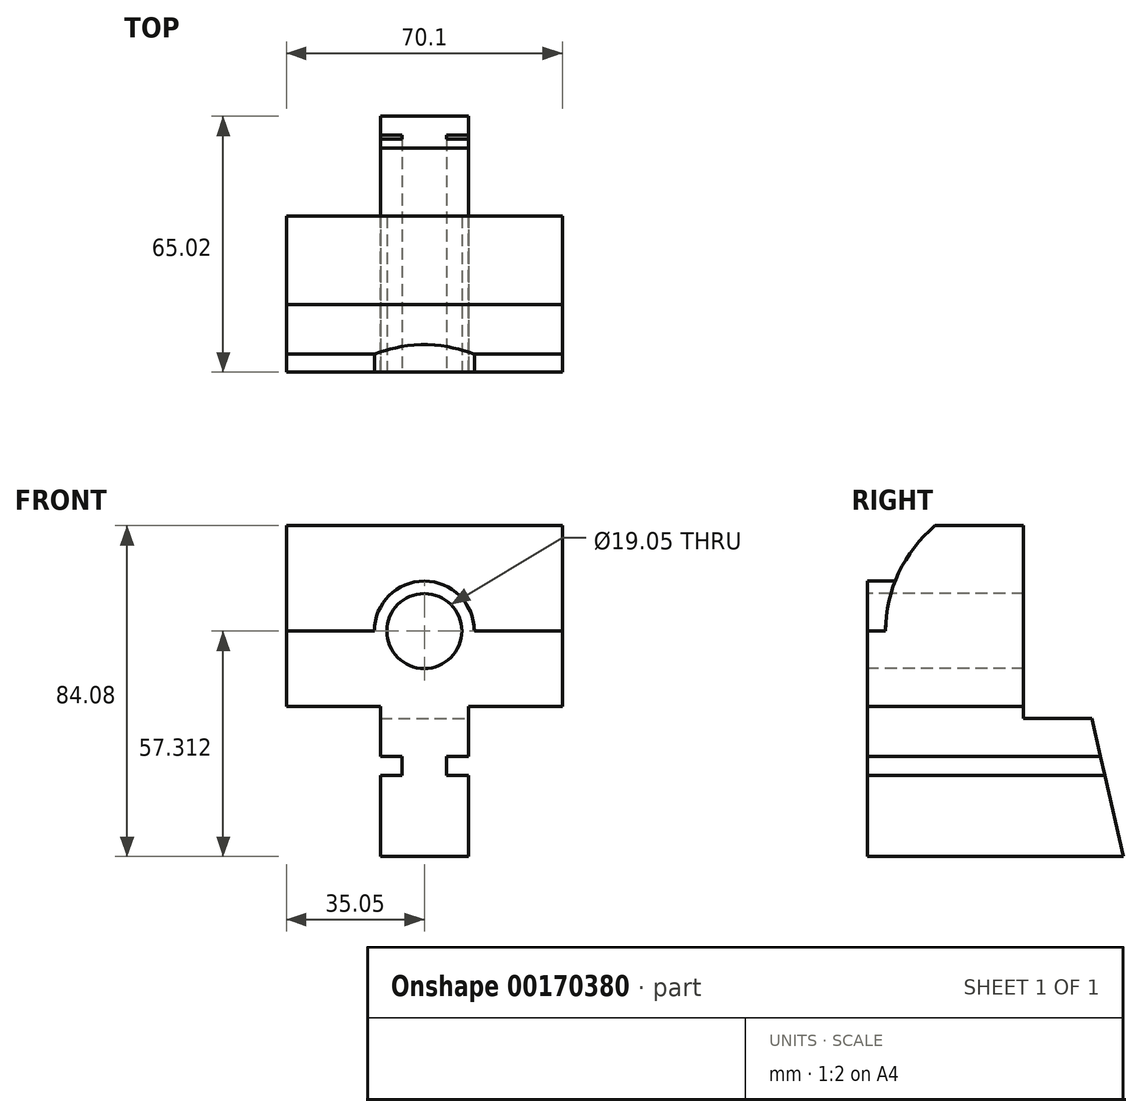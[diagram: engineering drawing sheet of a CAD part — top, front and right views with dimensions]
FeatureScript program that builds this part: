
annotation { "Feature Type Name" : "Feature", "Feature Type Description" : "" }
export const myFeature = defineFeature(function(context is Context, id is Id, definition is map)
    precondition{}
    {
        {
            var Q0;
            Q0=qCreatedBy(makeId("Right.planeOp"),FACE);
            var sketch = newSketch(context, id + "F0", { "sketchPlane" : qUnion([Q0])});
            skLineSegment(sketch, "E0.bottom", {"start": v(32.51, 42.04) * mm, "end": v(-32.51, 42.04) * mm});
            skLineSegment(sketch, "E0.top", {"start": v(32.51, -42.04) * mm, "end": v(-32.51, -42.04) * mm});
            skLineSegment(sketch, "E0.left", {"start": v(32.51, 42.04) * mm, "end": v(32.51, -42.04) * mm});
            skLineSegment(sketch, "E0.right", {"start": v(-32.51, 42.04) * mm, "end": v(-32.51, -42.04) * mm});
            skPoint(sketch, "E0.middle", {"position": v(0, 0) * mm});
            skSolve(sketch);
        }
        {
            var Q0;
            Q0 = qSketchRegion(id + "F0", true);
            extrude(context, id + "F1", {"entities" : qUnion([Q0]), "depth" : 35.05 * mm, "hasSecondDirection" : true, "secondDirectionOppositeDirection" : true, "secondDirectionDepth" : 35.05 * mm});
        }
        {
            var Q0;
            Q0=makeQuery(id+"F1.opExtrude","SWEPT_FACE",FACE,{"disambiguationData":[OSD([sQuery(id+"F0.wireOp",EDGE,"E0.right")])]});
            var sketch = newSketch(context, id + "F2", { "sketchPlane" : qUnion([Q0])});
            skLineSegment(sketch, "E1.bottom", {"start": v(-11.18, -3.94) * mm, "end": v(-74.28, -3.94) * mm});
            skLineSegment(sketch, "E1.top", {"start": v(-11.18, -51.01) * mm, "end": v(-74.28, -51.01) * mm});
            skLineSegment(sketch, "E1.left", {"start": v(-11.18, -3.94) * mm, "end": v(-11.18, -16.64) * mm});
            skLineSegment(sketch, "E1.right", {"start": v(-74.28, -3.94) * mm, "end": v(-74.28, -51.01) * mm});
            skLineSegment(sketch, "E2.bottom", {"start": v(11.18, -3.94) * mm, "end": v(76.81, -3.94) * mm});
            skLineSegment(sketch, "E2.top", {"start": v(11.18, -65.53) * mm, "end": v(76.81, -65.53) * mm});
            skLineSegment(sketch, "E2.left", {"start": v(11.18, -3.94) * mm, "end": v(11.18, -65.53) * mm});
            skLineSegment(sketch, "E2.right", {"start": v(76.81, -3.94) * mm, "end": v(76.81, -65.53) * mm});
            skLineSegment(sketch, "E3", {"start": v(-11.18, -16.64) * mm, "end": v(-5.59, -16.64) * mm});
            skLineSegment(sketch, "E4", {"start": v(-5.59, -16.64) * mm, "end": v(-5.59, -21.46) * mm});
            skLineSegment(sketch, "E5", {"start": v(-5.59, -21.46) * mm, "end": v(-11.18, -21.46) * mm});
            skLineSegment(sketch, "E6.trimOffspring", {"start": v(-11.18, -21.46) * mm, "end": v(-11.18, -51.01) * mm});
            skLineSegment(sketch, "E7", {"start": v(11.18, -16.64) * mm, "end": v(5.59, -16.64) * mm});
            skLineSegment(sketch, "E8", {"start": v(5.59, -16.64) * mm, "end": v(5.59, -21.46) * mm});
            skLineSegment(sketch, "E9", {"start": v(5.59, -21.46) * mm, "end": v(11.18, -21.46) * mm});
            skSolve(sketch);
        }
        {
            var Q0;
            Q0 = qSketchRegion(id + "F2", true);
            extrude(context, id + "F3", {"entities" : qUnion([Q0]), "operationType" : NewBodyOperationType.REMOVE, "endBound" : BoundingType.THROUGH_ALL, "oppositeDirection" : true, "depth" : 25.4 * mm});
        }
        {
            var Q0;
            Q0=makeQuery(id+"F1.opExtrude","CAP_FACE",FACE,{"disambiguationData":[OSD([sQuery(id+"F0.wireOp",EDGE,"E0.bottom"),sQuery(id+"F0.wireOp",EDGE,"E0.top"),sQuery(id+"F0.wireOp",EDGE,"E0.left"),sQuery(id+"F0.wireOp",EDGE,"E0.right")])],"isStart":false});
            var sketch = newSketch(context, id + "F4", { "sketchPlane" : qUnion([Q0])});
            skLineSegment(sketch, "E10.bottom", {"start": v(7.11, -6.99) * mm, "end": v(63.44, -6.99) * mm});
            skLineSegment(sketch, "E10.top", {"start": v(7.11, 61.83) * mm, "end": v(63.44, 61.83) * mm});
            skLineSegment(sketch, "E10.left", {"start": v(7.11, -6.99) * mm, "end": v(7.11, 61.83) * mm});
            skLineSegment(sketch, "E10.right", {"start": v(63.44, -6.99) * mm, "end": v(63.44, 61.83) * mm});
            skSolve(sketch);
        }
        {
            var Q0;
            Q0 = qSketchRegion(id + "F4", true);
            extrude(context, id + "F5", {"entities" : qUnion([Q0]), "operationType" : NewBodyOperationType.REMOVE, "endBound" : BoundingType.SYMMETRIC, "oppositeDirection" : true, "depth" : 203.2 * mm});
        }
        {
            var Q0;
            {var subQ0=sQuery(id+"F2.wireOp",EDGE,"E2.left");Q0=makeQuery(id+"F3.boolean.opBoolean","COPY",FACE,{"derivedFrom":makeQuery(id+"F3.opExtrude","SWEPT_FACE",FACE,{"disambiguationData":[OSD([subQ0]),TDD([makeQuery(id+"F2.imprint","IMPRINT",EDGE,{"disambiguationData":[TD([[makeQuery(id+"F2.imprint","INTERSECT",VERTEX,{"derivedFrom":[subQ0,sQuery(id+"F2.wireOp",EDGE,"E9")]}),-1.0]])],"derivedFrom":subQ0}),makeQuery(id+"F2.imprint","IMPRINT",EDGE,{"disambiguationData":[TD([[makeQuery(id+"F2.imprint","INTERSECT",VERTEX,{"derivedFrom":[sQuery(id+"F2.wireOp",EDGE,"E2.top"),subQ0]}),1.0]])],"derivedFrom":subQ0})])]})});}
            var sketch = newSketch(context, id + "F6", { "sketchPlane" : qUnion([Q0])});
            skLineSegment(sketch, "E11", {"start": v(32.51, -42.04) * mm, "end": v(22.86, 0) * mm});
            skLineSegment(sketch, "E12", {"start": v(22.86, 0) * mm, "end": v(51.06, 0) * mm});
            skLineSegment(sketch, "E13", {"start": v(51.06, 0) * mm, "end": v(45.35, -62.61) * mm});
            skLineSegment(sketch, "E14", {"start": v(45.35, -62.61) * mm, "end": v(32.51, -42.04) * mm});
            skSolve(sketch);
        }
        {
            var Q0;
            Q0 = qSketchRegion(id + "F6", true);
            extrude(context, id + "F7", {"entities" : qUnion([Q0]), "operationType" : NewBodyOperationType.REMOVE, "endBound" : BoundingType.THROUGH_ALL, "oppositeDirection" : true, "depth" : 25.4 * mm});
        }
        {
            var Q0;
            Q0=qCreatedBy(makeId("Right.planeOp"),FACE);
            var sketch = newSketch(context, id + "F8", { "sketchPlane" : qUnion([Q0])});
            skCircle(sketch, "E15", {"center": v(7.11, 15.11) * mm, "radius": 35.05 * mm});
            skLineSegment(sketch, "E16", {"start": v(-27.94, 15.27) * mm, "end": v(-51.63, 15.27) * mm});
            skLineSegment(sketch, "E17", {"start": v(-51.63, 15.27) * mm, "end": v(-49.63, 54.34) * mm});
            skLineSegment(sketch, "E18", {"start": v(-49.63, 54.34) * mm, "end": v(7.15, 50.16) * mm});
            skSolve(sketch);
        }
        {
            var Q0;
            {var subQ0=sQuery(id+"F8.wireOp",EDGE,"E16");Q0=makeQuery(id+"F8.imprint","IMPRINT",FACE,{"disambiguationData":[TD([[makeQuery(id+"F8.imprint","IMPRINT",EDGE,{"derivedFrom":subQ0}),-1.0]])]});}
            extrude(context, id + "F9", {"entities" : qUnion([Q0]), "operationType" : NewBodyOperationType.REMOVE, "endBound" : BoundingType.SYMMETRIC, "oppositeDirection" : true, "depth" : 508 * mm});
        }
        {
            var Q0;
            Q0=makeQuery(id+"F1.opExtrude","SWEPT_FACE",FACE,{"disambiguationData":[OSD([sQuery(id+"F0.wireOp",EDGE,"E0.right")])]});
            var sketch = newSketch(context, id + "F10", { "sketchPlane" : qUnion([Q0])});
            skCircle(sketch, "E19", {"center": v(0, 15.27) * mm, "radius": 12.7 * mm});
            skCircle(sketch, "E20", {"center": v(0, 15.27) * mm, "radius": 9.53 * mm});
            skSolve(sketch);
        }
        {
            var Q0;
            {var subQ0=sQuery(id+"F10.wireOp",EDGE,"E19");var subQ1=makeQuery(id+"F9.boolean.opBoolean","INTERSECT",EDGE,{"derivedFrom":[makeQuery(id+"F1.opExtrude","SWEPT_FACE",FACE,{"disambiguationData":[OSD([sQuery(id+"F0.wireOp",EDGE,"E0.right")])]}),makeQuery(id+"F9.opExtrude","SWEPT_FACE",FACE,{"disambiguationData":[OSD([sQuery(id+"F8.wireOp",EDGE,"E16")])]})]});var subQ2=makeQuery(id+"F10.imprint","INTERSECT",VERTEX,{"disambiguationData":[OD(0.0)],"derivedFrom":[subQ1,subQ0]});Q0=makeQuery(id+"F10.imprint","IMPRINT",FACE,{"disambiguationData":[TD([[makeQuery(id+"F10.imprint","IMPRINT",EDGE,{"disambiguationData":[TD([[subQ2,1.0]])],"derivedFrom":subQ0}),1.0]])]});}
            var Q1;
            {var subQ0=sQuery(id+"F10.wireOp",EDGE,"E19");var subQ1=makeQuery(id+"F9.boolean.opBoolean","INTERSECT",EDGE,{"derivedFrom":[makeQuery(id+"F1.opExtrude","SWEPT_FACE",FACE,{"disambiguationData":[OSD([sQuery(id+"F0.wireOp",EDGE,"E0.right")])]}),makeQuery(id+"F9.opExtrude","SWEPT_FACE",FACE,{"disambiguationData":[OSD([sQuery(id+"F8.wireOp",EDGE,"E16")])]})]});var subQ2=makeQuery(id+"F10.imprint","INTERSECT",VERTEX,{"disambiguationData":[OD(0.0)],"derivedFrom":[subQ1,subQ0]});Q1=makeQuery(id+"F10.imprint","IMPRINT",FACE,{"disambiguationData":[TD([[makeQuery(id+"F10.imprint","IMPRINT",EDGE,{"disambiguationData":[TD([[subQ2,-1.0]])],"derivedFrom":subQ0}),1.0]])]});}
            extrude(context, id + "F11", {"entities" : qUnion([Q0, Q1]), "operationType" : NewBodyOperationType.ADD, "oppositeDirection" : true, "depth" : 25.4 * mm});
        }
        {
            var Q0;
            {var subQ0=sQuery(id+"F10.wireOp",EDGE,"E20");var subQ1=makeQuery(id+"F9.boolean.opBoolean","INTERSECT",EDGE,{"derivedFrom":[makeQuery(id+"F1.opExtrude","SWEPT_FACE",FACE,{"disambiguationData":[OSD([sQuery(id+"F0.wireOp",EDGE,"E0.right")])]}),makeQuery(id+"F9.opExtrude","SWEPT_FACE",FACE,{"disambiguationData":[OSD([sQuery(id+"F8.wireOp",EDGE,"E16")])]})]});var subQ2=makeQuery(id+"F10.imprint","INTERSECT",VERTEX,{"disambiguationData":[OD(0.0)],"derivedFrom":[subQ1,subQ0]});Q0=makeQuery(id+"F10.imprint","IMPRINT",FACE,{"disambiguationData":[TD([[makeQuery(id+"F10.imprint","IMPRINT",EDGE,{"disambiguationData":[TD([[subQ2,1.0]])],"derivedFrom":subQ0}),1.0]])]});}
            var Q1;
            {var subQ0=sQuery(id+"F10.wireOp",EDGE,"E20");var subQ1=makeQuery(id+"F9.boolean.opBoolean","INTERSECT",EDGE,{"derivedFrom":[makeQuery(id+"F1.opExtrude","SWEPT_FACE",FACE,{"disambiguationData":[OSD([sQuery(id+"F0.wireOp",EDGE,"E0.right")])]}),makeQuery(id+"F9.opExtrude","SWEPT_FACE",FACE,{"disambiguationData":[OSD([sQuery(id+"F8.wireOp",EDGE,"E16")])]})]});var subQ2=makeQuery(id+"F10.imprint","INTERSECT",VERTEX,{"disambiguationData":[OD(0.0)],"derivedFrom":[subQ1,subQ0]});Q1=makeQuery(id+"F10.imprint","IMPRINT",FACE,{"disambiguationData":[TD([[makeQuery(id+"F10.imprint","IMPRINT",EDGE,{"disambiguationData":[TD([[subQ2,-1.0]])],"derivedFrom":subQ0}),1.0]])]});}
            extrude(context, id + "F12", {"entities" : qUnion([Q0, Q1]), "operationType" : NewBodyOperationType.REMOVE, "endBound" : BoundingType.THROUGH_ALL, "oppositeDirection" : true, "depth" : 25.4 * mm});
        }
    });
